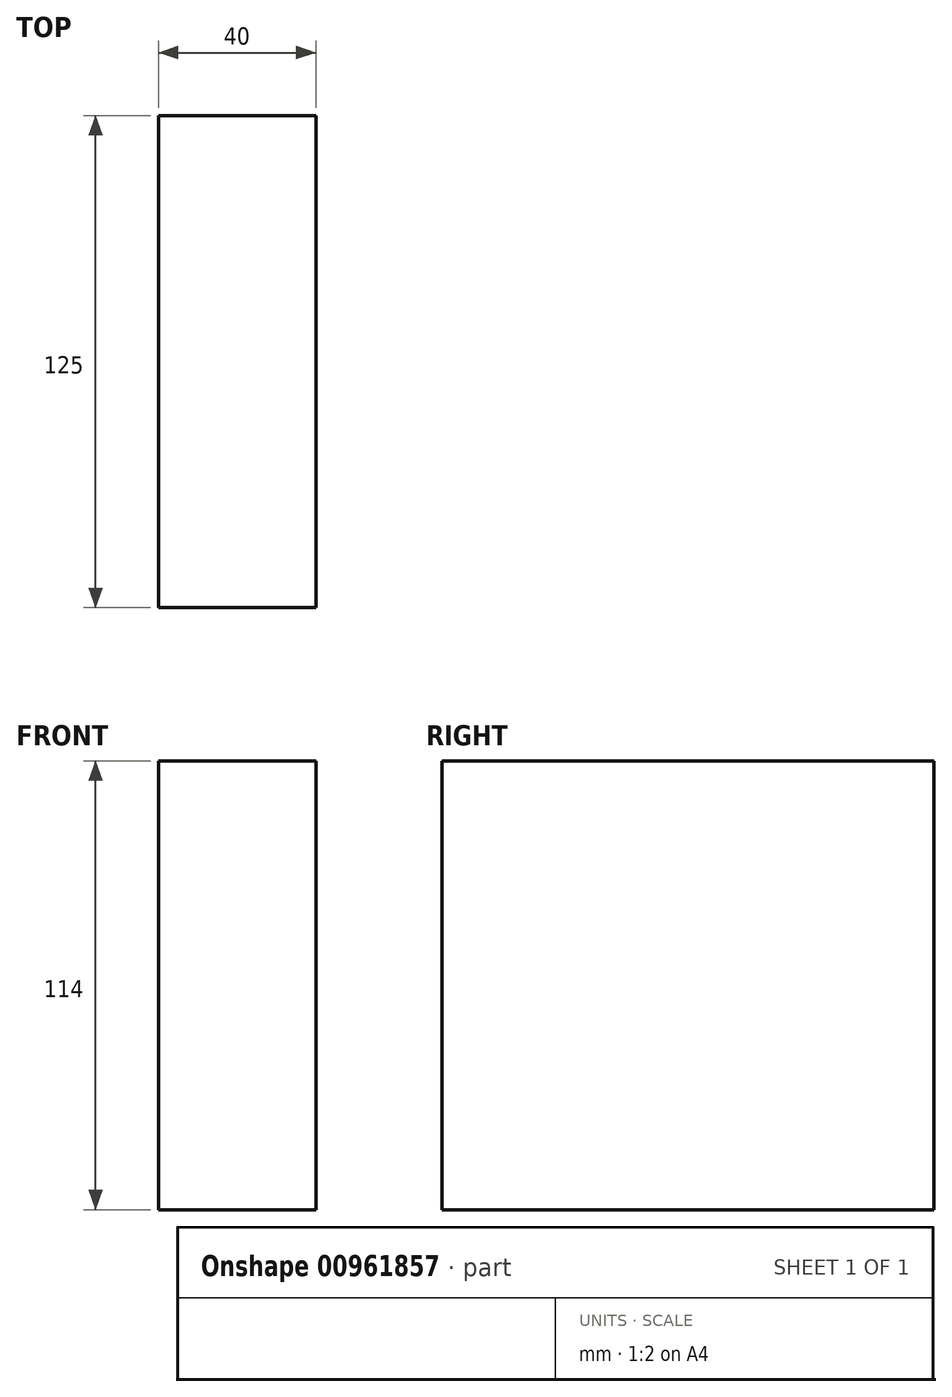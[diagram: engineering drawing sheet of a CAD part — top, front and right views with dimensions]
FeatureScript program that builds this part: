
annotation { "Feature Type Name" : "Feature", "Feature Type Description" : "" }
export const myFeature = defineFeature(function(context is Context, id is Id, definition is map)
    precondition{}
    {
        {
            var Q0;
            Q0=qCreatedBy(makeId("Top.planeOp"),FACE);
            var sketch = newSketch(context, id + "F0", { "sketchPlane" : qUnion([Q0])});
            skLineSegment(sketch, "E0.bottom", {"start": v(-91.37, 83.69) * mm, "end": v(-51.37, 83.69) * mm});
            skLineSegment(sketch, "E0.top", {"start": v(-91.37, -41.31) * mm, "end": v(-51.37, -41.31) * mm});
            skLineSegment(sketch, "E0.left", {"start": v(-91.37, 83.69) * mm, "end": v(-91.37, -41.31) * mm});
            skLineSegment(sketch, "E0.right", {"start": v(-51.37, 83.69) * mm, "end": v(-51.37, -41.31) * mm});
            skSolve(sketch);
        }
        {
            var Q0;
            Q0 = qSketchRegion(id + "F0", true);
            extrude(context, id + "F1", {"entities" : qUnion([Q0]), "depth" : 114 * mm, "offsetDistance" : 25 * mm});
        }
    });
